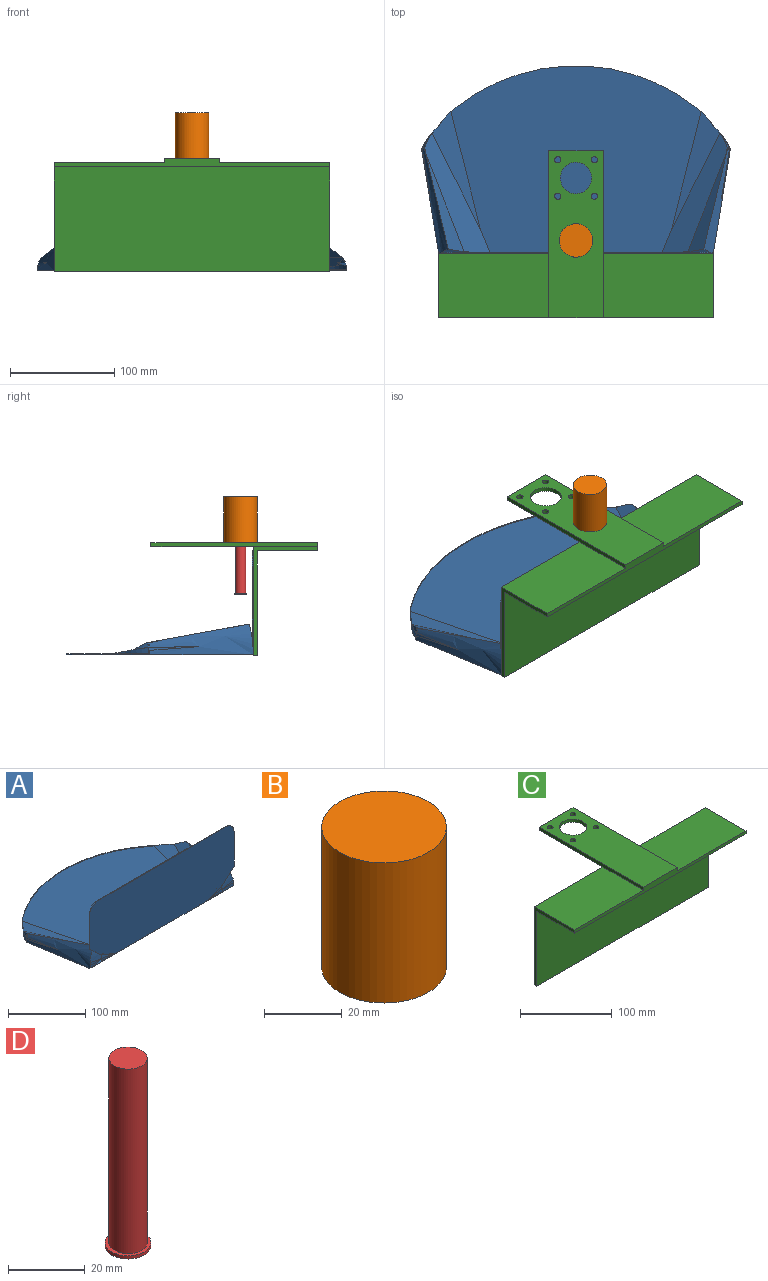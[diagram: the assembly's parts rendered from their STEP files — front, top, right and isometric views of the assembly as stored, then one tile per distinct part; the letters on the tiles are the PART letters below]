
ASSEMBLY  parts=4 mates=3
PART A: 66 faces, bbox 317.9x184.7x102 mm
  f0: revolved ~4.97x1.24mm, area 0.5mm2, adj f3,f12,f34,f59
  f1: plane 27.01x2.05mm, normal (0,0,1), area 0.2mm2, adj f5,f7,f39,f40,f50,f60
  f2: plane 26.68x1.72mm, normal (0,0,1), area 0.2mm2, adj f3,f7,f12,f14,f30,f59
  f3: cone r=0mm half-angle=67.1deg, axis (0.39,0.92,0), area 65.3mm2, adj f0,f2,f12,f59
  f4: revolved ~4.97x1.24mm, area 0.5mm2, adj f5,f6,f39,f60
  f5: cone r=0mm half-angle=67.1deg, axis (-0.39,0.92,0), area 65.3mm2, adj f1,f4,f39,f60
  f6: revolved ~29.59x26.08mm, area 434.2mm2, adj f4,f27,f37,f39,f40,f43,f50,f52
  f7: plane 264x100mm, normal (0,-1,0), area 25176.2mm2, adj f1,f2,f27,f30,f50,f56,f57,f59
  f8: plane 1.06x0.17mm, normal (-0.99,-0.16,0), area 0.1mm2, adj f10,f26,f51
  f9: revolved ~25.08x10.51mm, area 1.7mm2, adj f19,f21,f34,f36,f58
  f10: plane 297.01x179.72mm, normal (0,0,1), area 34898.8mm2, adj f8,f11,f13,f16,f18,f21,f22,f23
  f11: plane 114.58x57.38mm, normal (-0.17,0.04,0.98), area 1350.4mm2, adj f10,f15,f18,f20,f21,f28,f29,f32
  f12: plane 44.88x7.67mm, normal (-0.17,0.04,0.98), area 1.9mm2, adj f0,f2,f3,f14,f17,f34
  f13: plane 1.06x0.17mm, normal (0.99,-0.16,0), area 0.1mm2, adj f10,f22,f31
  f14: cone r=0mm half-angle=76deg, axis (0.24,0.97,0), area 83mm2, adj f2,f12,f17,f30,f34
  f15: cone r=49.92mm half-angle=4.6deg, axis (-0.24,-0.97,0), area 73.3mm2, adj f11,f18,f32
  f16: cone r=49.92mm half-angle=4.6deg, axis (-0.24,-0.97,0), area 0.6mm2, adj f10,f18,f31
  f17: cone r=49.92mm half-angle=4.6deg, axis (-0.24,-0.97,0), area 0.1mm2, adj f12,f14,f34
  f18: revolved ~22.07x16.79mm, area 122.3mm2, adj f10,f11,f15,f16,f28,f31,f32
  f19: cone r=0mm half-angle=67.1deg, axis (0.39,0.92,0), area 11.8mm2, adj f9,f21,f58
  f20: cone r=47.41mm half-angle=13.5deg, axis (-0.39,-0.92,0), area 7.8mm2, adj f11,f21,f29,f33,f36
  f21: plane 113.81x62.72mm, normal (-0.46,0.19,0.87), area 2491.8mm2, adj f9,f10,f11,f19,f20,f29,f36,f58
  f22: cylinder r=64mm len=22mm, axis (0,0,-1), area 27.7mm2, adj f10,f13,f23,f27
  f23: cylinder r=64mm len=18mm, axis (0,0,-1), area 24.6mm2, adj f10,f22,f24,f27
  f24: cylinder r=186.36mm len=230mm, axis (0,0,-1), area 247.9mm2, adj f10,f23,f25,f27
  f25: cylinder r=64mm len=18mm, axis (0,0,-1), area 24.6mm2, adj f10,f24,f26,f27
  f26: cylinder r=64mm len=22mm, axis (0,0,-1), area 27.7mm2, adj f8,f10,f25,f27
  f27: plane 296x179.71mm, normal (0,0,-1), area 44861.6mm2, adj f6,f7,f22,f23,f24,f25,f26,f32
  f28: revolved ~13.98x11.63mm, area 18mm2, adj f10,f11,f18
  f29: revolved ~14.38x9.15mm, area 35.6mm2, adj f11,f20,f21
  f30: revolved ~4.48x0.22mm, area 0.1mm2, adj f2,f7,f14,f34
  f31: revolved ~5.1x0.44mm, area 0.7mm2, adj f10,f13,f16,f18,f32
  f32: revolved ~101.76x29.59mm, area 2146.5mm2, adj f11,f15,f18,f27,f31,f33,f34,f35
  f33: revolved ~4.63x2.3mm, area 6.6mm2, adj f11,f20,f32,f36
  f34: revolved ~29.59x26.08mm, area 434.2mm2, adj f0,f9,f12,f14,f17,f27,f30,f32
  f35: plane 0.09x0.03mm, normal (-0.59,0.25,0.77), area 0mm2, adj f32,f34,f36
  f36: bspline ~104.02x50.73mm, area 1056.3mm2, adj f9,f20,f21,f32,f33,f34,f35
  f37: revolved ~25.08x10.51mm, area 1.7mm2, adj f6,f45,f47,f55,f58
  f38: plane 114.58x57.38mm, normal (0.17,0.04,0.98), area 1350.4mm2, adj f10,f41,f44,f46,f47,f48,f49,f52
  f39: plane 44.88x7.67mm, normal (0.17,0.04,0.98), area 1.9mm2, adj f1,f4,f5,f6,f40,f43
  f40: cone r=0mm half-angle=76deg, axis (-0.24,0.97,0), area 83mm2, adj f1,f6,f39,f43,f50
  f41: cone r=49.92mm half-angle=4.6deg, axis (0.24,-0.97,0), area 73.3mm2, adj f38,f44,f52
  f42: cone r=49.92mm half-angle=4.6deg, axis (0.24,-0.97,0), area 0.6mm2, adj f10,f44,f51
  f43: cone r=49.92mm half-angle=4.6deg, axis (0.24,-0.97,0), area 0.1mm2, adj f6,f39,f40
  f44: revolved ~22.07x16.79mm, area 122.3mm2, adj f10,f38,f41,f42,f48,f51,f52
  f45: cone r=0mm half-angle=67.1deg, axis (-0.39,0.92,0), area 11.8mm2, adj f37,f47,f58
  f46: cone r=47.41mm half-angle=13.5deg, axis (0.39,-0.92,0), area 7.8mm2, adj f38,f47,f49,f53,f55
  f47: plane 113.81x62.72mm, normal (0.46,0.19,0.87), area 2491.8mm2, adj f10,f37,f38,f45,f46,f49,f55,f58
  f48: revolved ~13.98x11.63mm, area 18mm2, adj f10,f38,f44
  f49: revolved ~14.38x9.15mm, area 35.6mm2, adj f38,f46,f47
  f50: revolved ~4.48x0.22mm, area 0.1mm2, adj f1,f6,f7,f40
  f51: revolved ~5.1x0.44mm, area 0.7mm2, adj f8,f10,f42,f44,f52
  f52: revolved ~101.76x29.59mm, area 2146.6mm2, adj f6,f27,f38,f41,f44,f51,f53,f54
  f53: revolved ~4.63x2.3mm, area 6.6mm2, adj f38,f46,f52,f55
  f54: plane 0.09x0.03mm, normal (0.59,0.25,0.77), area 0mm2, adj f6,f52,f55
  f55: bspline ~104.02x50.73mm, area 1056.3mm2, adj f6,f37,f46,f47,f52,f53,f54
  f56: plane 21.43x19.83mm, normal (0.68,0,-0.73), area 28.5mm2, adj f7,f34,f58,f59,f65
  f57: plane 21.43x19.83mm, normal (-0.68,0,-0.73), area 28.5mm2, adj f6,f7,f58,f60,f61
  f58: plane 264.33x99.33mm, normal (0,1,0), area 24809.4mm2, adj f6,f9,f10,f19,f21,f34,f37,f45
  f59: plane 25.03x9.71mm, normal (0.36,0,-0.93), area 10.5mm2, adj f0,f2,f3,f7,f34,f56
  f60: plane 25.03x9.71mm, normal (-0.36,0,-0.93), area 10.5mm2, adj f1,f4,f5,f6,f7,f57
  f61: plane 54.46x1mm, normal (-1,0,0), area 54.5mm2, adj f7,f57,f58,f62
  f62: cylinder r=15mm len=15mm, axis (0,-1,0), area 23.6mm2, adj f7,f58,f61,f63
  f63: plane 234x1mm, normal (0,0,1), area 234mm2, adj f7,f58,f62,f64
  f64: cylinder r=15mm len=15mm, axis (0,-1,0), area 23.6mm2, adj f7,f58,f63,f65
  f65: plane 54.46x1mm, normal (1,0,0), area 54.5mm2, adj f7,f56,f58,f64
PART B: 3 faces, bbox 32x32x44 mm
  f0: cylinder r=16mm len=44mm, axis (0,0,-1), area 4423.4mm2, adj f1,f2
  f1: plane 32x32mm, normal (0,0,1), area 804.2mm2, adj f0
  f2: plane 32x32mm, normal (0,0,-1), area 804.2mm2, adj f0
PART C: 19 faces, bbox 264x160x108 mm
  f0: plane 106x62mm, normal (0,0,1), area 6572mm2, adj f2,f6,f7,f12
  f1: plane 106x62mm, normal (0,0,1), area 6572mm2, adj f2,f6,f8,f11
  f2: plane 264x8mm, normal (0,-1,0), area 1264mm2, adj f0,f1,f3,f7,f8,f11,f12,f13
  f3: plane 264x58mm, normal (0,0,-1), area 15312mm2, adj f2,f4,f7,f8
  f4: plane 264x100mm, normal (0,-1,0), area 26400mm2, adj f3,f5,f7,f8
  f5: plane 264x4mm, normal (0,0,-1), area 1056mm2, adj f4,f6,f7,f8
  f6: plane 264x104mm, normal (0,1,0), area 27456mm2, adj f0,f1,f5,f7,f8,f9
  f7: plane 104x62mm, normal (1,0,0), area 648mm2, adj f0,f2,f3,f4,f5,f6
  f8: plane 104x62mm, normal (-1,0,0), area 648mm2, adj f1,f2,f3,f4,f5,f6
  f9: plane 98x52mm, normal (0,0,-1), area 4276mm2, adj f6,f10,f11,f12,f14,f15,f16,f17
  f10: plane 52x4mm, normal (0,1,0), area 208mm2, adj f9,f11,f12,f13
  f11: plane 160x4mm, normal (-1,0,0), area 640mm2, adj f1,f2,f9,f10,f13
  f12: plane 160x4mm, normal (1,0,0), area 640mm2, adj f0,f2,f9,f10,f13
  f13: plane 160x52mm, normal (0,0,1), area 7500mm2, adj f2,f10,f11,f12,f14,f15,f16,f17
  f14: cylinder r=15mm len=30mm, axis (0,0,1), area 377mm2, adj f9,f13
  f15: cylinder r=3mm len=6mm, axis (0,0,1), area 75.4mm2, adj f9,f13
  f16: cylinder r=3mm len=6mm, axis (0,0,1), area 75.4mm2, adj f9,f13
  f17: cylinder r=3mm len=6mm, axis (0,0,1), area 75.4mm2, adj f9,f13
  f18: cylinder r=3mm len=6mm, axis (0,0,1), area 75.4mm2, adj f9,f13
PART D: 5 faces, bbox 12x12x60 mm
  f0: cylinder r=5mm len=59mm, axis (0,0,1), area 1853.5mm2, adj f1,f4
  f1: plane 10x10mm, normal (0,0,1), area 78.5mm2, adj f0
  f2: cylinder r=6mm len=12mm, axis (0,0,1), area 37.7mm2, adj f3,f4
  f3: plane 12x12mm, normal (0,0,-1), area 113.1mm2, adj f2
  f4: plane 12x12mm, normal (0,0,1), area 34.6mm2, adj f0,f2
PLACE A at identity
PLACE B t=(0,-33.6,-0.37)mm
PLACE C t=(0,0.31,-0.37)mm
PLACE D t=(0,-33.6,9.63)mm
MATE slider D.f0 <-> B.f0  axis (0,0,1) through (-148,-608.23,117.63)mm
MATE fastened C.f6 <-> A.f7  axis (0,1,0) through (-148,-620.33,51.63)mm
MATE fastened C.f13 <-> B.f0  axis (0,0,1) through (-148,-608.23,107.63)mm
